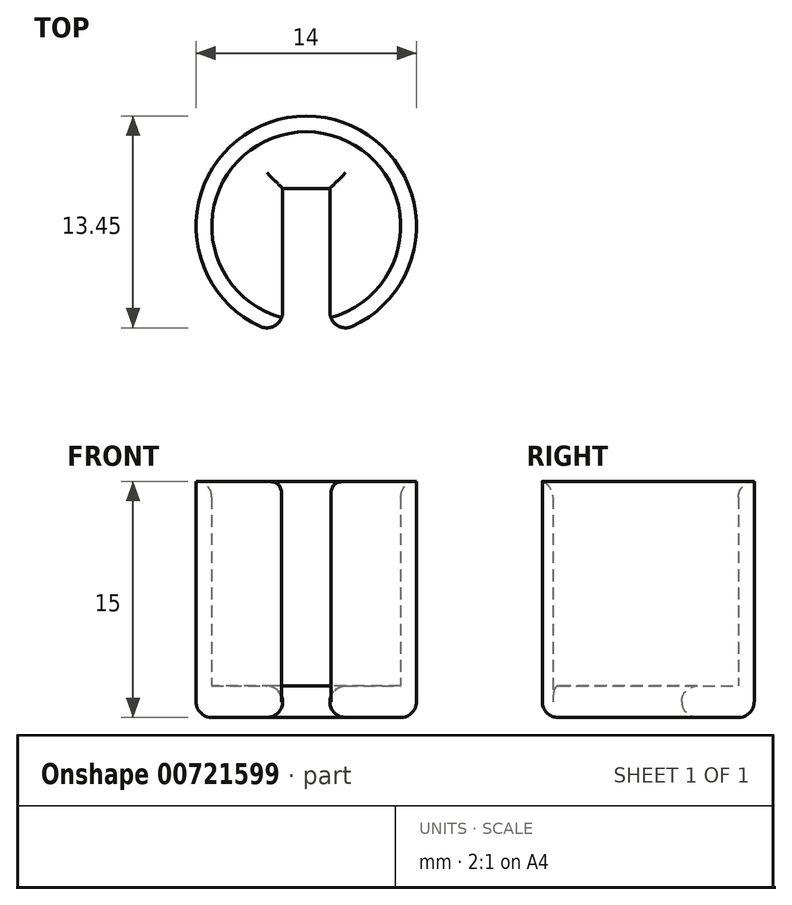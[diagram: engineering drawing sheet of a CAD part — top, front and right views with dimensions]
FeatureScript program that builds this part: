
annotation { "Feature Type Name" : "Feature", "Feature Type Description" : "" }
export const myFeature = defineFeature(function(context is Context, id is Id, definition is map)
    precondition{}
    {
        {
            var Q0;
            Q0=qCreatedBy(makeId("Top.planeOp"),FACE);
            var sketch = newSketch(context, id + "F0", { "sketchPlane" : qUnion([Q0])});
            skArc(sketch, "E0", {"start": v(1.5, -5.8) * mm, "mid": v(0, 6) * mm, "end": v(-1.5, -5.8) * mm});
            skArc(sketch, "E1", {"start": v(1.5, -6.84) * mm, "mid": v(0, 7) * mm, "end": v(-1.5, -6.84) * mm});
            skLineSegment(sketch, "E2", {"start": v(0, 2.4) * mm, "end": v(1.5, 2.4) * mm});
            skLineSegment(sketch, "E3", {"start": v(1.5, 2.4) * mm, "end": v(1.5, -6.84) * mm});
            skLineSegment(sketch, "E4", {"start": v(0, 2.4) * mm, "end": v(-1.5, 2.4) * mm});
            skLineSegment(sketch, "E5", {"start": v(-1.5, 2.4) * mm, "end": v(-1.5, -5.8) * mm});
            skLineSegment(sketch, "E6", {"start": v(-1.5, -5.8) * mm, "end": v(-1.5, -6.84) * mm});
            skSolve(sketch);
        }
        {
            var Q0;
            {var subQ1=sQuery(id+"F0.wireOp",EDGE,"E0");Q0=makeQuery(id+"F0.imprint","IMPRINT",FACE,{"disambiguationData":[TD([[makeQuery(id+"F0.imprint","IMPRINT",EDGE,{"derivedFrom":subQ1}),1.0]])]});}
            extrude(context, id + "F1", {"entities" : qUnion([Q0]), "depth" : 2 * mm, "offsetDistance" : 25 * mm});
        }
        {
            var Q0;
            {var subQ0=sQuery(id+"F0.wireOp",EDGE,"E0");Q0=makeQuery(id+"F0.imprint","IMPRINT",FACE,{"disambiguationData":[TD([[makeQuery(id+"F0.imprint","IMPRINT",EDGE,{"derivedFrom":subQ0}),-1.0]])]});}
            extrude(context, id + "F2", {"entities" : qUnion([Q0]), "operationType" : NewBodyOperationType.ADD, "depth" : 15 * mm, "offsetDistance" : 25 * mm});
        }
        {
            var Q0;
            Q0=makeQuery(id+"F2.opExtrude","SWEPT_EDGE",EDGE,{"disambiguationData":[OSD([sQuery(id+"F0.wireOp",EDGE,"E1"),sQuery(id+"F0.wireOp",EDGE,"E3")])]});
            var Q1;
            Q1=makeQuery(id+"F2.opExtrude","SWEPT_EDGE",EDGE,{"disambiguationData":[OSD([sQuery(id+"F0.wireOp",EDGE,"E1"),sQuery(id+"F0.wireOp",EDGE,"E6")])]});
            var Q2;
            {var subQ0=sQuery(id+"F0.wireOp",EDGE,"E3");Q2=makeQuery(id+"F2.boolean.opBoolean","MERGE",EDGE,{"derivedFrom":[makeQuery(id+"F1.opExtrude","CAP_EDGE",EDGE,{"disambiguationData":[OSD([subQ0])],"isStart":true}),makeQuery(id+"F2.opExtrude","CAP_EDGE",EDGE,{"disambiguationData":[OSD([subQ0])],"isStart":true})]});}
            var Q3;
            Q3=makeQuery(id+"F1.opExtrude","CAP_EDGE",EDGE,{"disambiguationData":[OSD([sQuery(id+"F0.wireOp",EDGE,"E2"),sQuery(id+"F0.wireOp",EDGE,"E4")])],"isStart":true});
            var Q4;
            Q4=makeQuery(id+"F2.boolean.opBoolean","MERGE",EDGE,{"derivedFrom":[makeQuery(id+"F1.opExtrude","CAP_EDGE",EDGE,{"disambiguationData":[OSD([sQuery(id+"F0.wireOp",EDGE,"E5")])],"isStart":true}),makeQuery(id+"F2.opExtrude","CAP_EDGE",EDGE,{"disambiguationData":[OSD([sQuery(id+"F0.wireOp",EDGE,"E6")])],"isStart":true})]});
            fillet(context, id + "F3", {"entities" : qUnion([Q0, Q1, Q2, Q3, Q4]), "radius" : 1 * mm, "tangentPropagation" : true, "allowEdgeOverflow" : false});
        }
        {
            var Q0;
            Q0=makeQuery(id+"F2.opExtrude","CAP_EDGE",EDGE,{"disambiguationData":[OSD([sQuery(id+"F0.wireOp",EDGE,"E1")])],"isStart":true});
            fillet(context, id + "F4", {"entities" : qUnion([Q0]), "radius" : 1 * mm, "tangentPropagation" : true, "allowEdgeOverflow" : false});
        }
        {
            var Q0;
            Q0=makeQuery(id+"F2.opExtrude","CAP_EDGE",EDGE,{"disambiguationData":[OSD([sQuery(id+"F0.wireOp",EDGE,"E0")])],"isStart":false});
            fillet(context, id + "F5", {"entities" : qUnion([Q0]), "radius" : 1 * mm, "tangentPropagation" : true, "allowEdgeOverflow" : false});
        }
        {
            var Q0;
            Q0=makeQuery(id+"F1.opExtrude","CAP_EDGE",EDGE,{"disambiguationData":[OSD([sQuery(id+"F0.wireOp",EDGE,"E2"),sQuery(id+"F0.wireOp",EDGE,"E4")])],"isStart":false});
            var Q1;
            Q1=makeQuery(id+"F1.opExtrude","CAP_EDGE",EDGE,{"disambiguationData":[OSD([sQuery(id+"F0.wireOp",EDGE,"E3")])],"isStart":false});
            fillet(context, id + "F6", {"entities" : qUnion([Q0, Q1]), "radius" : 1 * mm, "tangentPropagation" : true, "allowEdgeOverflow" : false});
        }
        {
            var Q0;
            Q0=makeQuery(id+"F1.opExtrude","CAP_EDGE",EDGE,{"disambiguationData":[OSD([sQuery(id+"F0.wireOp",EDGE,"E5")])],"isStart":false});
            fillet(context, id + "F7", {"entities" : qUnion([Q0]), "radius" : 1 * mm, "tangentPropagation" : true, "allowEdgeOverflow" : false});
        }
    });
